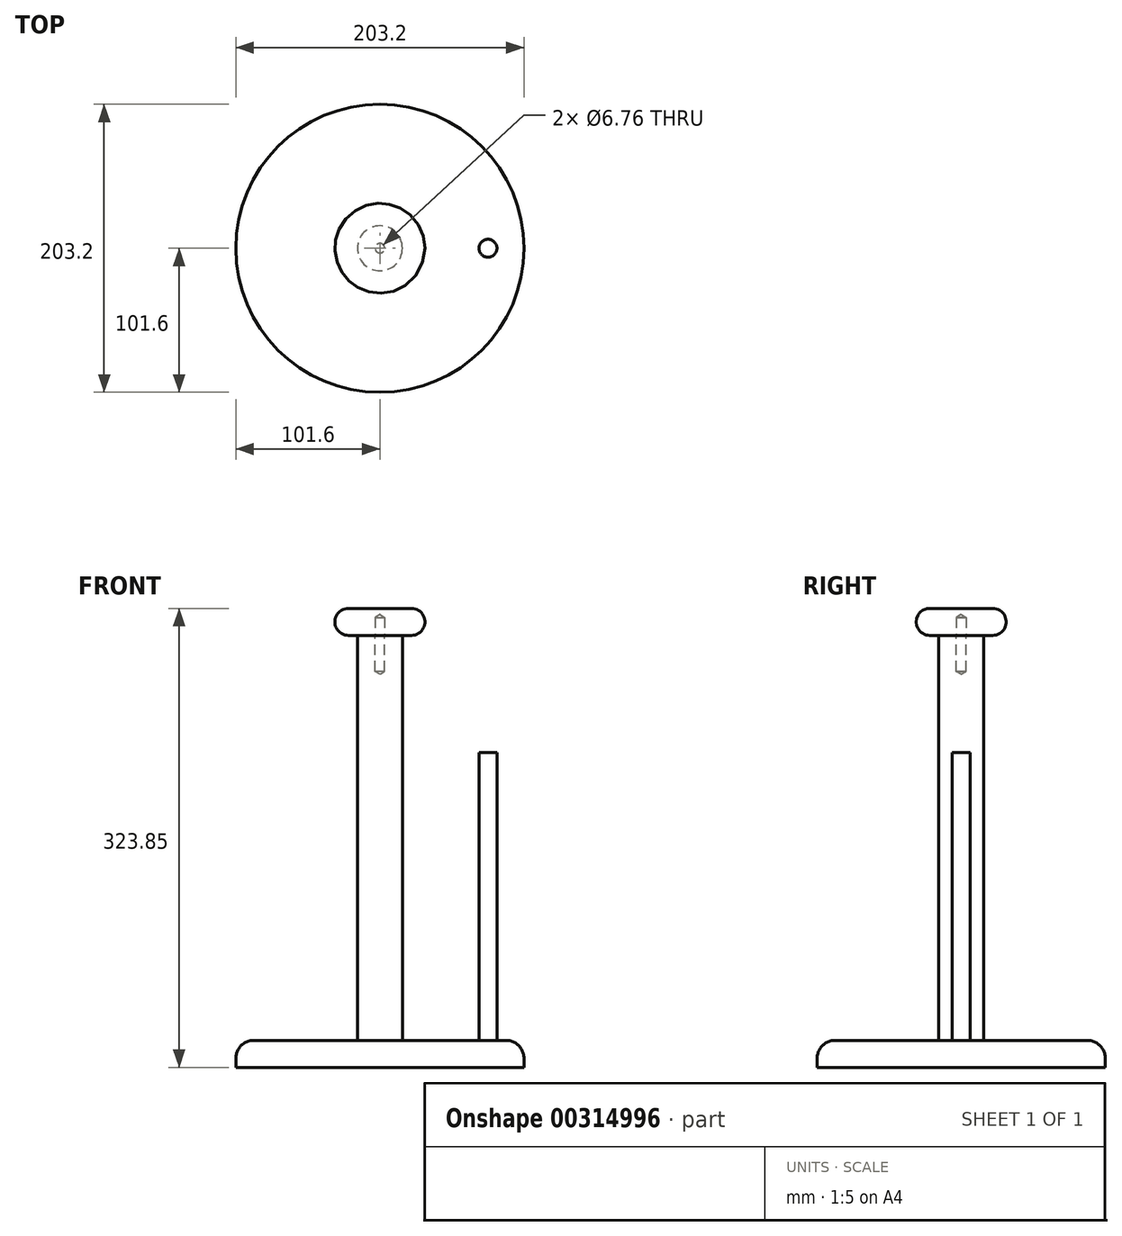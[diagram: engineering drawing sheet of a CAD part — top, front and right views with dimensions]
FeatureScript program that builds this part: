
annotation { "Feature Type Name" : "Feature", "Feature Type Description" : "" }
export const myFeature = defineFeature(function(context is Context, id is Id, definition is map)
    precondition{}
    {
        {
            var Q0;
            Q0=qCreatedBy(makeId("Top.planeOp"),FACE);
            var sketch = newSketch(context, id + "F0", { "sketchPlane" : qUnion([Q0])});
            skCircle(sketch, "E0", {"center": v(0, 0) * mm, "radius": 101.6 * mm});
            skSolve(sketch);
        }
        {
            var Q0;
            Q0 = qSketchRegion(id + "F0", true);
            extrude(context, id + "F1", {"entities" : qUnion([Q0]), "depth" : 19.05 * mm});
        }
        {
            var Q0;
            Q0=makeQuery(id+"F1.opExtrude","CAP_EDGE",EDGE,{"disambiguationData":[OSD([sQuery(id+"F0.wireOp",EDGE,"E0")])],"isStart":false});
            fillet(context, id + "F2", {"entities" : qUnion([Q0]), "radius" : 12.7 * mm, "tangentPropagation" : true, "allowEdgeOverflow" : false});
        }
        {
            var Q0;
            Q0=makeQuery(id+"F1.opExtrude","CAP_FACE",FACE,{"disambiguationData":[OSD([sQuery(id+"F0.wireOp",EDGE,"E0")])],"isStart":false});
            var sketch = newSketch(context, id + "F3", { "sketchPlane" : qUnion([Q0])});
            skCircle(sketch, "E1", {"center": v(0, 0) * mm, "radius": 15.88 * mm});
            skCircle(sketch, "E2", {"center": v(76.2, 0) * mm, "radius": 6.35 * mm});
            skSolve(sketch);
        }
        {
            var Q0;
            Q0=makeQuery(id+"F3.imprint","IMPRINT",FACE,{"disambiguationData":[TD([[makeQuery(id+"F3.imprint","IMPRINT",EDGE,{"derivedFrom":sQuery(id+"F3.wireOp",EDGE,"E1")}),1.0]])]});
            extrude(context, id + "F4", {"entities" : qUnion([Q0]), "depth" : 285.75 * mm});
        }
        {
            var Q0;
            Q0=makeQuery(id+"F3.imprint","IMPRINT",FACE,{"disambiguationData":[TD([[makeQuery(id+"F3.imprint","IMPRINT",EDGE,{"derivedFrom":sQuery(id+"F3.wireOp",EDGE,"E2")}),1.0]])]});
            extrude(context, id + "F5", {"entities" : qUnion([Q0]), "depth" : 203.2 * mm});
        }
        {
            var Q0;
            Q0=makeQuery(id+"F4.opExtrude","CAP_FACE",FACE,{"disambiguationData":[OSD([sQuery(id+"F3.wireOp",EDGE,"E1")])],"isStart":false});
            var sketch = newSketch(context, id + "F6", { "sketchPlane" : qUnion([Q0])});
            skCircle(sketch, "E3", {"center": v(0, 0) * mm, "radius": 31.75 * mm});
            skSolve(sketch);
        }
        {
            var Q0;
            Q0 = qSketchRegion(id + "F6", true);
            extrude(context, id + "F7", {"entities" : qUnion([Q0]), "depth" : 19.05 * mm});
        }
        {
            var Q0;
            Q0=makeQuery(id+"F7.opExtrude","CAP_EDGE",EDGE,{"disambiguationData":[OSD([sQuery(id+"F6.wireOp",EDGE,"E3")])],"isStart":false});
            var Q1;
            Q1=makeQuery(id+"F7.opExtrude","CAP_EDGE",EDGE,{"disambiguationData":[OSD([sQuery(id+"F6.wireOp",EDGE,"E3")])],"isStart":true});
            fillet(context, id + "F8", {"entities" : qUnion([Q0, Q1]), "radius" : 9.52 * mm, "tangentPropagation" : true, "allowEdgeOverflow" : false});
        }
        {
            var Q0;
            Q0=sQuery(id+"F6.wireOp",VERTEX,"E3.center");
            var Q1;
            Q1=makeQuery(id+"F4.opExtrude","SWEPT_BODY",BODY,{"disambiguationData":[OSD([sQuery(id+"F3.wireOp",EDGE,"E1")])]});
            hole(context, id + "F9", {"style" : HoleStyle.SIMPLE, "endStyle" : HoleEndStyle.BLIND, "standardTappedOrClearance" : lookupTablePath({ "standard" : "ANSI", "fit" : "Normal (ASME)", "size" : "1/4", "type" : "Clearance" }), "standardBlindInLast" : lookupTablePath({ "fit" : "Free", "standard" : "ANSI", "size" : "1/4", "type" : "Clearance" }), "holeDiameter" : 6.76 * mm, "holeDepth" : 25.4 * mm, "tappedDepth" : 12.7 * mm, "tapClearance" : 3, "startFromSketch" : true, "locations" : qUnion([Q0]), "scope" : qUnion([Q1])});
        }
        {
            var Q0;
            Q0=sQuery(id+"F6.wireOp",VERTEX,"E3.center");
            var Q1;
            Q1=makeQuery(id+"F7.opExtrude","SWEPT_BODY",BODY,{"disambiguationData":[OSD([sQuery(id+"F6.wireOp",EDGE,"E3")])]});
            hole(context, id + "F10", {"style" : HoleStyle.SIMPLE, "endStyle" : HoleEndStyle.BLIND, "oppositeDirection" : true, "standardTappedOrClearance" : lookupTablePath({ "standard" : "ANSI", "fit" : "Normal (ASME)", "size" : "1/4", "type" : "Clearance" }), "standardBlindInLast" : lookupTablePath({ "fit" : "Free", "standard" : "ANSI", "size" : "1/4", "type" : "Clearance" }), "holeDiameter" : 6.76 * mm, "holeDepth" : 12.7 * mm, "tappedDepth" : 12.7 * mm, "tapClearance" : 3, "locations" : qUnion([Q0]), "scope" : qUnion([Q1])});
        }
    });
